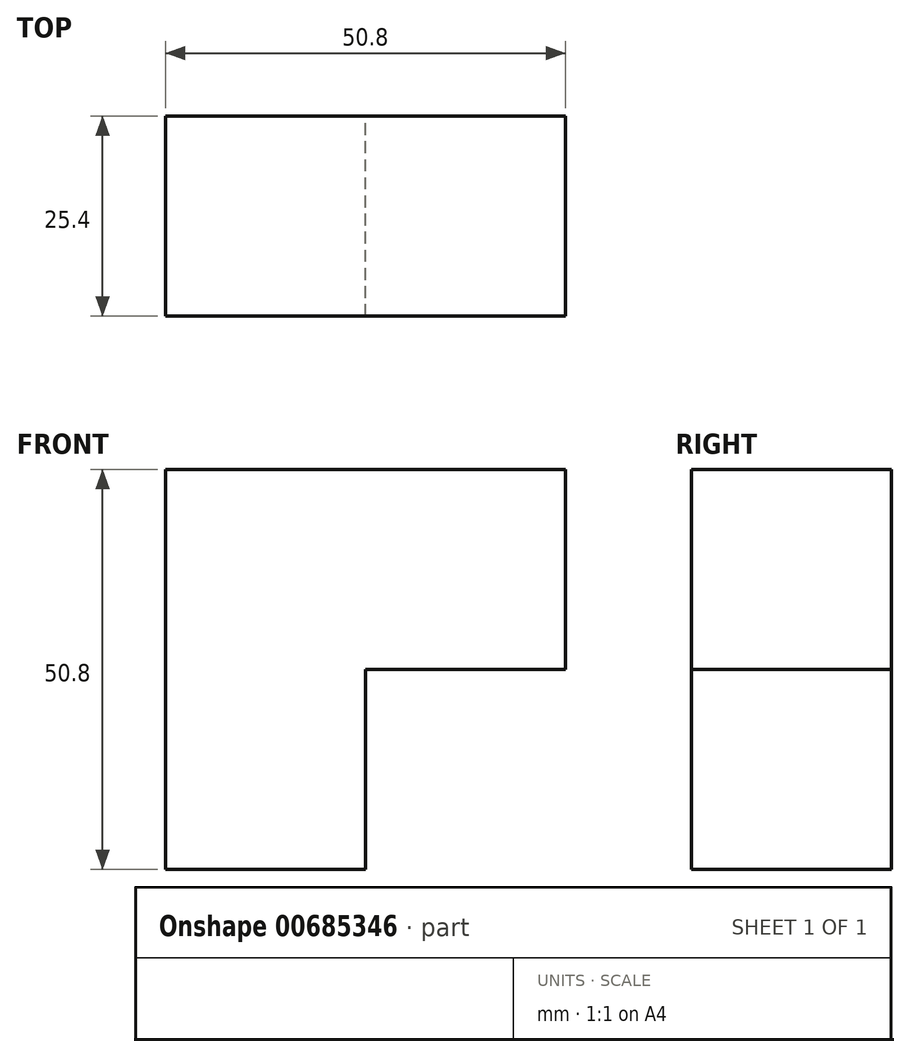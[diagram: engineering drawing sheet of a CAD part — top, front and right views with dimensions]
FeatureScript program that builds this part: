
annotation { "Feature Type Name" : "Feature", "Feature Type Description" : "" }
export const myFeature = defineFeature(function(context is Context, id is Id, definition is map)
    precondition{}
    {
        {
            var Q0;
            Q0=qCreatedBy(makeId("Front.planeOp"),FACE);
            var sketch = newSketch(context, id + "F0", { "sketchPlane" : qUnion([Q0])});
            skLineSegment(sketch, "E0", {"start": v(0, 0) * mm, "end": v(0, -25.4) * mm});
            skLineSegment(sketch, "E1", {"start": v(0, -25.4) * mm, "end": v(-25.4, -25.4) * mm});
            skLineSegment(sketch, "E2", {"start": v(-25.4, -25.4) * mm, "end": v(-25.4, 25.4) * mm});
            skLineSegment(sketch, "E3", {"start": v(-25.4, 25.4) * mm, "end": v(25.4, 25.4) * mm});
            skLineSegment(sketch, "E4", {"start": v(25.4, 25.4) * mm, "end": v(25.4, 0) * mm});
            skLineSegment(sketch, "E5", {"start": v(0, 0) * mm, "end": v(25.4, 0) * mm});
            skSolve(sketch);
        }
        {
            var Q0;
            Q0 = qSketchRegion(id + "F0", true);
            extrude(context, id + "F1", {"entities" : qUnion([Q0]), "depth" : 25.4 * mm, "offsetDistance" : 25.4 * mm});
        }
    });
